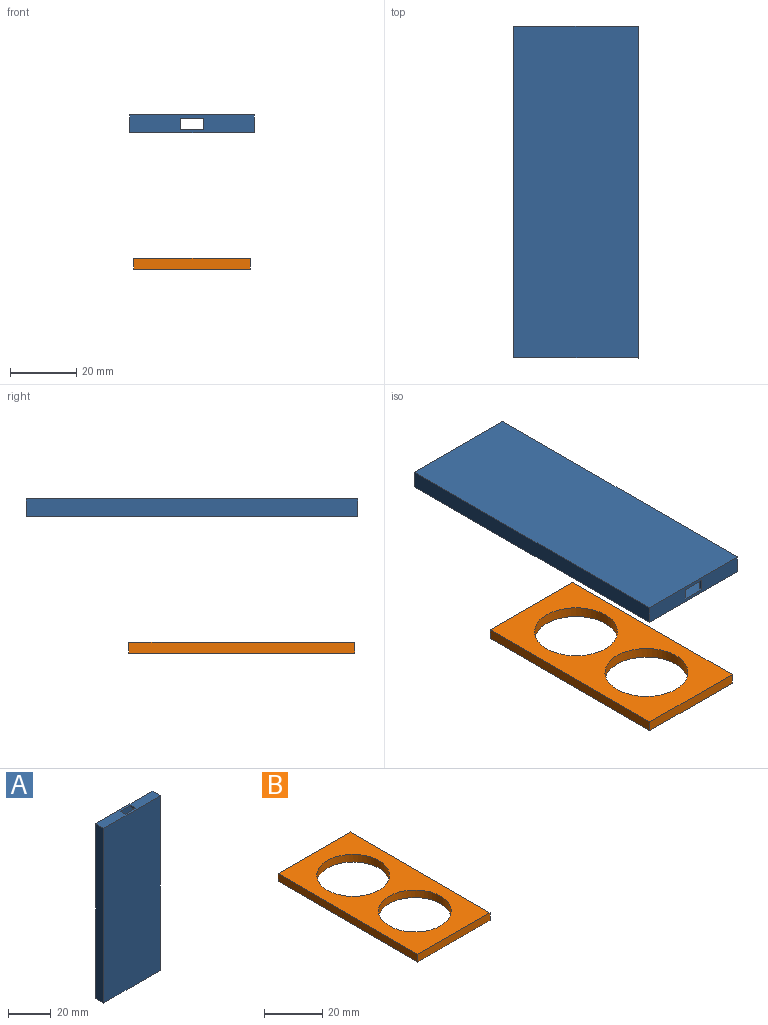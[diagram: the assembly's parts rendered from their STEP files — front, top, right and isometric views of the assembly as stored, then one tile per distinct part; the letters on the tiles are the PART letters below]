
ASSEMBLY  parts=2 mates=1
PART A: 19 faces, bbox 37.5x5.4x100 mm
  f0: plane 14.25x3.4mm, normal (0,0,-1), area 48.4mm2, adj f2,f3,f5,f18
  f1: plane 14.25x3.4mm, normal (0,0,1), area 48.4mm2, adj f2,f3,f5,f15
  f2: plane 98x3.4mm, normal (1,0,0), area 333.2mm2, adj f0,f1,f3,f5
  f3: plane 100x35.5mm, normal (0,1,0), area 3493mm2, adj f0,f1,f2,f4,f6,f7,f13,f14
  f4: plane 98x3.4mm, normal (-1,0,0), area 333.2mm2, adj f3,f5,f6,f7
  f5: plane 100x35.5mm, normal (0,-1,0), area 3002.1mm2, adj f0,f1,f2,f4,f6,f7,f8,f13
  f6: plane 14.25x3.4mm, normal (0,0,-1), area 48.4mm2, adj f3,f4,f5,f17
  f7: plane 14.25x3.4mm, normal (0,0,1), area 48.4mm2, adj f3,f4,f5,f16
  f8: cylinder r=12.5mm len=25mm, axis (0,1,0), area 78.5mm2, adj f5,f12
  f9: plane 100x5.4mm, normal (-1,0,0), area 540mm2, adj f10,f12,f13,f14
  f10: plane 100x37.5mm, normal (0,-1,0), area 3750mm2, adj f9,f11,f13,f14
  f11: plane 100x5.4mm, normal (1,0,0), area 540mm2, adj f10,f12,f13,f14
  f12: plane 100x37.5mm, normal (0,1,0), area 3259.1mm2, adj f8,f9,f11,f13,f14
  f13: plane 37.5x5.4mm, normal (0,0,1), area 178.7mm2, adj f3,f5,f9,f10,f11,f12,f17,f18
  f14: plane 37.5x5.4mm, normal (0,0,-1), area 178.7mm2, adj f3,f5,f9,f10,f11,f12,f15,f16
  f15: plane 3.4x1mm, normal (1,0,0), area 3.4mm2, adj f1,f3,f5,f14
  f16: plane 3.4x1mm, normal (-1,0,0), area 3.4mm2, adj f3,f5,f7,f14
  f17: plane 3.4x1mm, normal (-1,0,0), area 3.4mm2, adj f3,f5,f6,f13
  f18: plane 3.4x1mm, normal (1,0,0), area 3.4mm2, adj f0,f3,f5,f13
PART B: 8 faces, bbox 35x68x3.2 mm
  f0: plane 68x3.2mm, normal (-1,0,0), area 217.6mm2, adj f1,f3,f4,f5
  f1: plane 68x35mm, normal (0,0,-1), area 1398.3mm2, adj f0,f2,f4,f5,f6,f7
  f2: plane 68x3.2mm, normal (1,0,0), area 217.6mm2, adj f1,f3,f4,f5
  f3: plane 68x35mm, normal (0,0,1), area 1398.3mm2, adj f0,f2,f4,f5,f6,f7
  f4: plane 35x3.2mm, normal (0,-1,0), area 112mm2, adj f0,f1,f2,f3
  f5: plane 35x3.2mm, normal (0,1,0), area 112mm2, adj f0,f1,f2,f3
  f6: cylinder r=12.5mm len=25mm, axis (0,0,1), area 251.3mm2, adj f1,f3
  f7: cylinder r=12.5mm len=25mm, axis (0,0,1), area 251.3mm2, adj f1,f3
PLACE A rot(axis=(-1,0,0),90deg) t=(-66.36,-56.18,46.68)mm
PLACE B rot(axis=(-0.99,-0.04,-0.11),0deg) t=(-114.16,14.42,2.93)mm
MATE slider A.f8 <-> B.f7  axis (0,0,-1) through (-66.36,-6.18,43.98)mm
